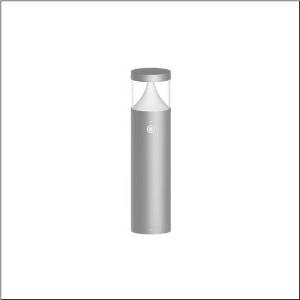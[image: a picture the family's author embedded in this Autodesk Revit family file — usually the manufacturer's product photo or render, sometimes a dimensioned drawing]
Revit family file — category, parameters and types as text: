
# Revit family: cl_31_poller_60_sensor_5cl434803
name_source: partatom
category: Lighting Fixtures
units: mm (PartAtom-declared; Revit-internal decimal feet)

## family parameters
Cut with Voids When Loaded = No
Host = Face
Light Source = No
Part Type = Normal
Room Calculation Point = No
Round Connector Dimension = Use Diameter
Shared = No

## types (1)
- --- (1 x LED, 1500 lm, 14 W, 3000K)
    Apparent Load = 14 VA
    CIE Flux Codes = 19 66 88 92 100
    Color Rendering = 80
    Color Temperature = 3000K
    Default Elevation = 1800 mm
    Description = CL 31 Bollard 60 Sensor, bollard luminaire, primary light control with lens, of PC, primary optical cover: cover panel, of PC, transparent, secondary light control with reflector, of PC, primary light characteristic: asymmetric, LED, rated luminous flux: 1.500lm, luminous efficacy: 107lm/W, light colour: 830, colour temperature: 3000K, control gear: DALI, with terminal, 5-pole, max. 2.5mm², mains connection: 220..240V, AC, 50/60Hz, rated input power: 14W, luminaire housing, of aluminium, powder-coated, SITECO metallic grey, diameter: 170mm, height: 600mm, PIR sensor, protection rating (complete): IP65, insulation class (complete): insulation class I (protective earthing), certification: CE, ENEC, impact resistance: IK08, permissible operating ambient temperature for outdoor applications: -20..+50°C, packaging unit: 1 piece
    Height = 200 mm  [stored 0.656168 ft]
    Lamp = 1 x LED
    Lamp Light Flux = 1500 lm
    Lamp Power = 14 W
    Lamp count = 1
    Length = 170 mm  [stored 0.557743 ft]
    Luminous efficacy = 107 lm/W
    Manufacturer = Siteco
    ModVariant = No
    Model = 5CL434803
    Mounting Place = Floor
    Mounting Type = Freestanding
    Number of Poles = 1
    OnlyDefault = Yes
    Power Factor = 1
    Product Name = CL 31 Poller 60 Sensor
    Product group = bollard luminaire
    ProductGroupID = 1304
    Protection Class = Protection class I
    Protection Degree = IP 65
    RLX_Detail_Level = 1
    RLX_Emergency_Light_Flux = 0 lm
    RLX_Emergency_Type = 0
    RLX_Emergency_Type_DB = No
    RlxData = <blob elided: 64473 chars, md5=640bead9>
    Socket = socket
    Standby Power = 0 W
    System Light Flux = 1500 lm
    System Power = 14 W
    Type Comments = factory setting: luminous flux: 100 % | dim-lin: 254 | 350 mA
    Type Image = l_1006901.jpg
    URL = http://relux.com
    VarID = @adj_192629
    Voltage = 0 V
    Weight = 0.00 kg
    Width = 0 mm  [stored 0 ft]

note: [stored X ft] marks values corroborated as IEEE doubles in the binary element streams (Revit-internal decimal feet)

## geometry (parser evidence)
native form markers: Blend x4, Sweep x13
no freeform markers — native parametric forms only
